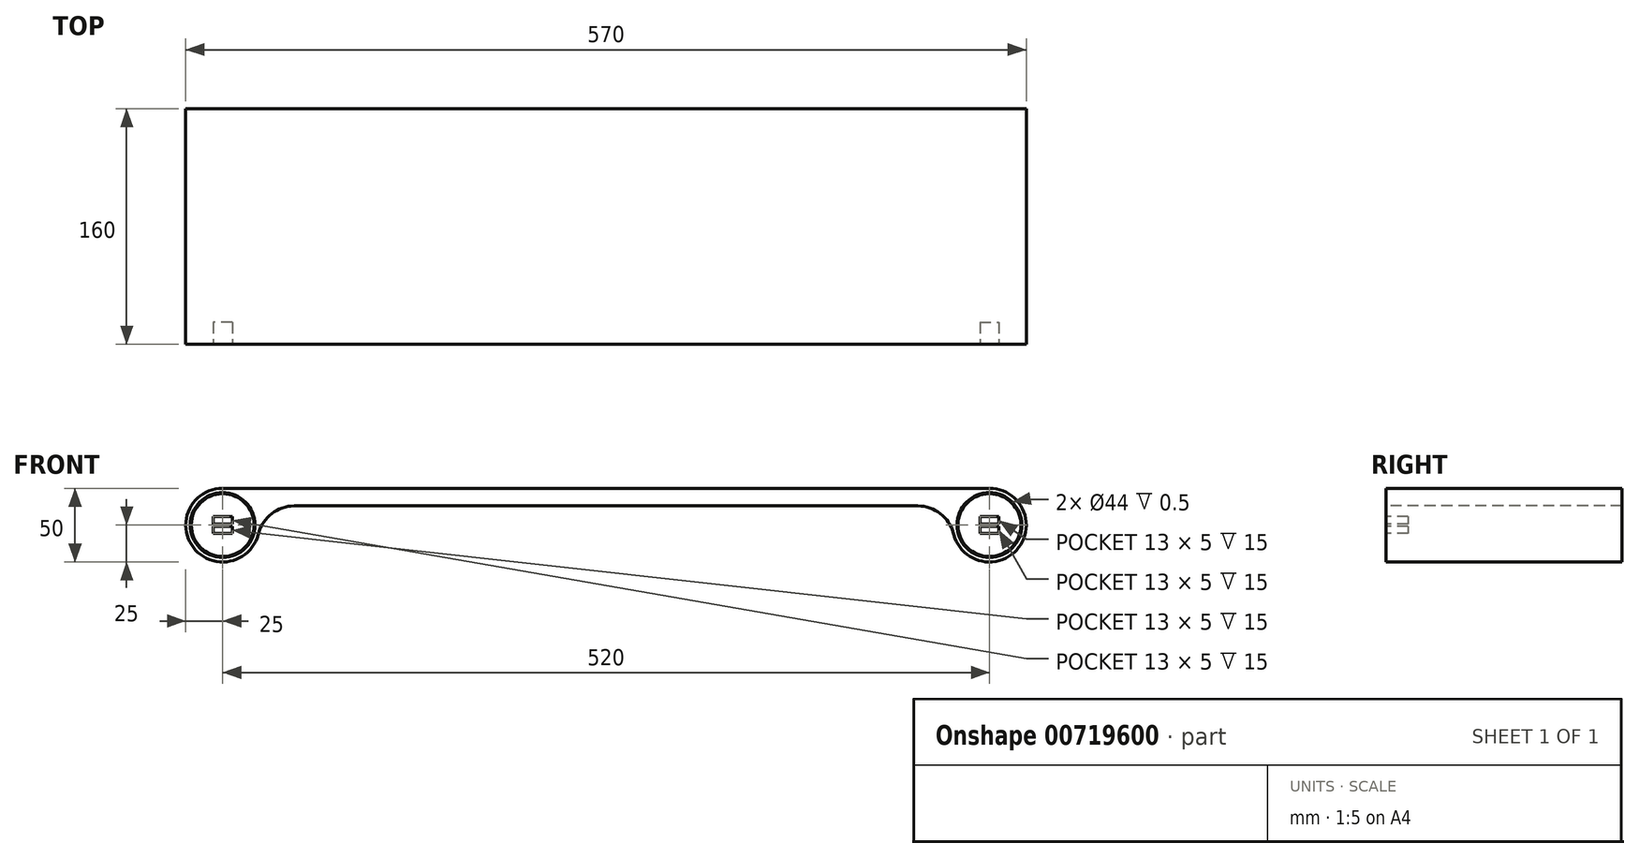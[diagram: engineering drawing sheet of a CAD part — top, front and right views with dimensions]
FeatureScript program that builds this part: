
annotation { "Feature Type Name" : "Feature", "Feature Type Description" : "" }
export const myFeature = defineFeature(function(context is Context, id is Id, definition is map)
    precondition{}
    {
        {
            var Q0;
            Q0=qCreatedBy(makeId("Front.planeOp"),FACE);
            var sketch = newSketch(context, id + "F0", { "sketchPlane" : qUnion([Q0])});
            skLineSegment(sketch, "E0", {"start": v(0, 0) * mm, "end": v(0, 50) * mm, "construction": true});
            skArc(sketch, "E1", {"start": v(235.85, 18.53) * mm, "mid": v(279.83, 9.78) * mm, "end": v(260, 50) * mm});
            skLineSegment(sketch, "E2", {"start": v(260, 50) * mm, "end": v(0, 50) * mm});
            skLineSegment(sketch, "E3.0", {"start": v(211.45, 38) * mm, "end": v(0, 38) * mm});
            skLineSegment(sketch, "E4", {"start": v(235.85, 18.53) * mm, "end": v(235.6, 19.47) * mm});
            skPoint(sketch, "E5.visualSharp", {"position": v(230.63, 38) * mm});
            skArc(sketch, "E5.filletArc", {"start": v(235.6, 19.47) * mm, "mid": v(226.67, 32.83) * mm, "end": v(211.45, 38) * mm});
            skLineSegment(sketch, "E6.MirrorCS", {"start": v(-260, 50) * mm, "end": v(0, 50) * mm});
            skArc(sketch, "E7.MirrorCS", {"start": v(-235.85, 18.53) * mm, "mid": v(-279.83, 9.78) * mm, "end": v(-260, 50) * mm});
            skLineSegment(sketch, "E8.MirrorCS", {"start": v(-235.85, 18.53) * mm, "end": v(-235.6, 19.47) * mm});
            skArc(sketch, "E9.MirrorCS", {"start": v(-235.6, 19.47) * mm, "mid": v(-226.67, 32.83) * mm, "end": v(-211.45, 38) * mm});
            skLineSegment(sketch, "E10.MirrorCS", {"start": v(-211.45, 38) * mm, "end": v(0, 38) * mm});
            skSolve(sketch);
        }
        {
            var Q0;
            Q0=makeQuery(id+"F0.imprint","IMPRINT",FACE,{"disambiguationData":[TD([[makeQuery(id+"F0.imprint","IMPRINT",EDGE,{"derivedFrom":sQuery(id+"F0.wireOp",EDGE,"E1")}),1.0]])]});
            extrude(context, id + "F1", {"entities" : qUnion([Q0]), "oppositeDirection" : true, "depth" : 160 * mm, "offsetDistance" : 25 * mm});
        }
        {
            var Q0;
            Q0=makeQuery(id+"F1.opExtrude","CAP_FACE",FACE,{"disambiguationData":[OSD([sQuery(id+"F0.wireOp",EDGE,"E1"),sQuery(id+"F0.wireOp",EDGE,"E2"),sQuery(id+"F0.wireOp",EDGE,"E3.0"),sQuery(id+"F0.wireOp",EDGE,"E4"),sQuery(id+"F0.wireOp",EDGE,"E5.filletArc"),sQuery(id+"F0.wireOp",EDGE,"E6.MirrorCS"),sQuery(id+"F0.wireOp",EDGE,"E7.MirrorCS"),sQuery(id+"F0.wireOp",EDGE,"E8.MirrorCS"),sQuery(id+"F0.wireOp",EDGE,"E9.MirrorCS"),sQuery(id+"F0.wireOp",EDGE,"E10.MirrorCS")])],"isStart":true});
            var sketch = newSketch(context, id + "F2", { "sketchPlane" : qUnion([Q0])});
            skCircle(sketch, "E11", {"center": v(260, 25) * mm, "radius": 22 * mm});
            skCircle(sketch, "E12", {"center": v(260, 25) * mm, "radius": 21.25 * mm});
            skCircle(sketch, "E13.MirrorC", {"center": v(-260, 25) * mm, "radius": 22 * mm});
            skCircle(sketch, "E14.MirrorC", {"center": v(-260, 25) * mm, "radius": 21.25 * mm});
            skSolve(sketch);
        }
        {
            var Q0;
            Q0 = qSketchRegion(id + "F2", true);
            extrude(context, id + "F3", {"entities" : qUnion([Q0]), "operationType" : NewBodyOperationType.REMOVE, "oppositeDirection" : true, "depth" : .5 * mm, "offsetDistance" : 25 * mm});
        }
        {
            var Q0;
            Q0=makeQuery(id+"F3.boolean.opBoolean","SPLIT",FACE,{"disambiguationData":[TD([makeQuery(id+"F3.opExtrude","SWEPT_FACE",FACE,{"disambiguationData":[OSD([sQuery(id+"F2.wireOp",EDGE,"E12")])]})])],"derivedFrom":makeQuery(id+"F1.opExtrude","CAP_FACE",FACE,{"disambiguationData":[OSD([sQuery(id+"F0.wireOp",EDGE,"E1"),sQuery(id+"F0.wireOp",EDGE,"E2"),sQuery(id+"F0.wireOp",EDGE,"E3.0"),sQuery(id+"F0.wireOp",EDGE,"E4"),sQuery(id+"F0.wireOp",EDGE,"E5.filletArc"),sQuery(id+"F0.wireOp",EDGE,"E6.MirrorCS"),sQuery(id+"F0.wireOp",EDGE,"E7.MirrorCS"),sQuery(id+"F0.wireOp",EDGE,"E8.MirrorCS"),sQuery(id+"F0.wireOp",EDGE,"E9.MirrorCS"),sQuery(id+"F0.wireOp",EDGE,"E10.MirrorCS")])],"isStart":true})});
            var sketch = newSketch(context, id + "F4", { "sketchPlane" : qUnion([Q0])});
            skLineSegment(sketch, "E15.bottom", {"start": v(253.5, 30.75) * mm, "end": v(266.5, 30.75) * mm});
            skLineSegment(sketch, "E15.top", {"start": v(253.5, 25.75) * mm, "end": v(266.5, 25.75) * mm});
            skLineSegment(sketch, "E15.left", {"start": v(253.5, 30.75) * mm, "end": v(253.5, 25.75) * mm});
            skLineSegment(sketch, "E15.right", {"start": v(266.5, 30.75) * mm, "end": v(266.5, 25.75) * mm});
            skLineSegment(sketch, "E16.bottom", {"start": v(253.5, 24.25) * mm, "end": v(266.5, 24.25) * mm});
            skLineSegment(sketch, "E16.top", {"start": v(253.5, 19.25) * mm, "end": v(266.5, 19.25) * mm});
            skLineSegment(sketch, "E16.left", {"start": v(253.5, 24.25) * mm, "end": v(253.5, 19.25) * mm});
            skLineSegment(sketch, "E16.right", {"start": v(266.5, 24.25) * mm, "end": v(266.5, 19.25) * mm});
            skPoint(sketch, "E17", {"position": v(260, 25) * mm});
            skLineSegment(sketch, "E18", {"start": v(260, 25.75) * mm, "end": v(260, 24.25) * mm, "construction": true});
            skLineSegment(sketch, "E19.MirrorCS", {"start": v(-253.5, 30.75) * mm, "end": v(-266.5, 30.75) * mm});
            skLineSegment(sketch, "E20.MirrorCS", {"start": v(-253.5, 30.75) * mm, "end": v(-253.5, 25.75) * mm});
            skLineSegment(sketch, "E21.MirrorCS", {"start": v(-266.5, 30.75) * mm, "end": v(-266.5, 25.75) * mm});
            skLineSegment(sketch, "E22.MirrorCS", {"start": v(-253.5, 25.75) * mm, "end": v(-266.5, 25.75) * mm});
            skLineSegment(sketch, "E23.MirrorCS", {"start": v(-253.5, 24.25) * mm, "end": v(-266.5, 24.25) * mm});
            skLineSegment(sketch, "E24.MirrorCS", {"start": v(-266.5, 24.25) * mm, "end": v(-266.5, 19.25) * mm});
            skLineSegment(sketch, "E25.MirrorCS", {"start": v(-253.5, 19.25) * mm, "end": v(-266.5, 19.25) * mm});
            skLineSegment(sketch, "E26.MirrorCS", {"start": v(-253.5, 24.25) * mm, "end": v(-253.5, 19.25) * mm});
            skSolve(sketch);
        }
        {
            var Q0;
            Q0=makeQuery(id+"F4.imprint","IMPRINT",FACE,{"disambiguationData":[TD([[makeQuery(id+"F4.imprint","IMPRINT",EDGE,{"derivedFrom":sQuery(id+"F4.wireOp",EDGE,"E15.bottom")}),-1.0]])]});
            var Q1;
            Q1=makeQuery(id+"F4.imprint","IMPRINT",FACE,{"disambiguationData":[TD([[makeQuery(id+"F4.imprint","IMPRINT",EDGE,{"derivedFrom":sQuery(id+"F4.wireOp",EDGE,"E16.bottom")}),-1.0]])]});
            var Q2;
            Q2=makeQuery(id+"F4.imprint","IMPRINT",FACE,{"disambiguationData":[TD([[makeQuery(id+"F4.imprint","IMPRINT",EDGE,{"derivedFrom":sQuery(id+"F4.wireOp",EDGE,"E19.MirrorCS")}),1.0]])]});
            var Q3;
            Q3=makeQuery(id+"F4.imprint","IMPRINT",FACE,{"disambiguationData":[TD([[makeQuery(id+"F4.imprint","IMPRINT",EDGE,{"derivedFrom":sQuery(id+"F4.wireOp",EDGE,"E23.MirrorCS")}),1.0]])]});
            extrude(context, id + "F5", {"entities" : qUnion([Q0, Q1, Q2, Q3]), "operationType" : NewBodyOperationType.REMOVE, "oppositeDirection" : true, "depth" : 15 * mm, "offsetDistance" : 25 * mm});
        }
    });
